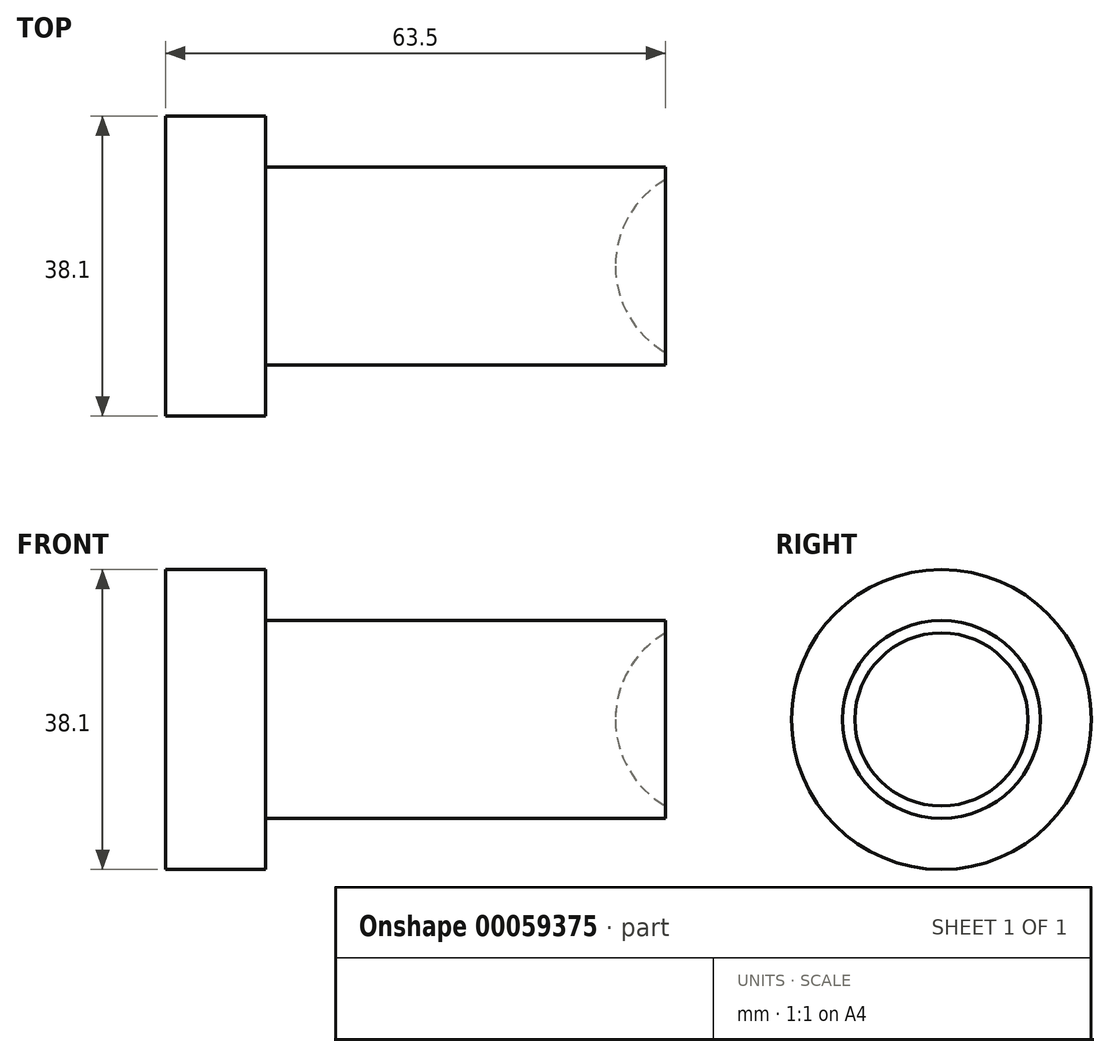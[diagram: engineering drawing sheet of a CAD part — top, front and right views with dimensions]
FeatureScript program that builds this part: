
annotation { "Feature Type Name" : "Feature", "Feature Type Description" : "" }
export const myFeature = defineFeature(function(context is Context, id is Id, definition is map)
    precondition{}
    {
        {
            var Q0;
            Q0=qCreatedBy(makeId("Front.planeOp"),FACE);
            var sketch = newSketch(context, id + "F0", { "sketchPlane" : qUnion([Q0])});
            skLineSegment(sketch, "E0.bottom", {"start": v(0, 0) * mm, "end": v(12.7, 0) * mm});
            skLineSegment(sketch, "E0.top", {"start": v(0, 19.05) * mm, "end": v(12.7, 19.05) * mm});
            skLineSegment(sketch, "E0.left", {"start": v(0, 0) * mm, "end": v(0, 19.05) * mm});
            skLineSegment(sketch, "E0.right", {"start": v(12.7, 0) * mm, "end": v(12.7, 19.05) * mm});
            skLineSegment(sketch, "E1.bottom", {"start": v(12.7, 0) * mm, "end": v(57.15, 0) * mm});
            skLineSegment(sketch, "E1.top", {"start": v(12.7, 12.57) * mm, "end": v(63.5, 12.57) * mm});
            skLineSegment(sketch, "E1.left", {"start": v(12.7, 0) * mm, "end": v(12.7, 12.57) * mm});
            skLineSegment(sketch, "E1.right", {"start": v(63.5, 11) * mm, "end": v(63.5, 12.57) * mm});
            skArc(sketch, "E2", {"start": v(63.5, 11) * mm, "mid": v(58.85, 6.35) * mm, "end": v(57.15, 0) * mm});
            skPoint(sketch, "E3.orphan", {"position": v(63.5, 0) * mm});
            skSolve(sketch);
        }
        {
            var Q0;
            Q0 = qSketchRegion(id + "F0", true);
            var Q1;
            Q1=makeQuery(id+"F0.imprint","IMPRINT",FACE,{"disambiguationData":[TD([[makeQuery(id+"F0.imprint","IMPRINT",EDGE,{"derivedFrom":sQuery(id+"F0.wireOp",EDGE,"E1.bottom")}),1.0]])]});
            var Q2;
            Q2=sQuery(id+"F0.wireOp",EDGE,"E1.bottom");
            revolve(context, id + "F1", {"entities" : qUnion([Q0, Q1]), "axis" : qUnion([Q2]), "revolveType" : RevolveType.FULL});
        }
    });
